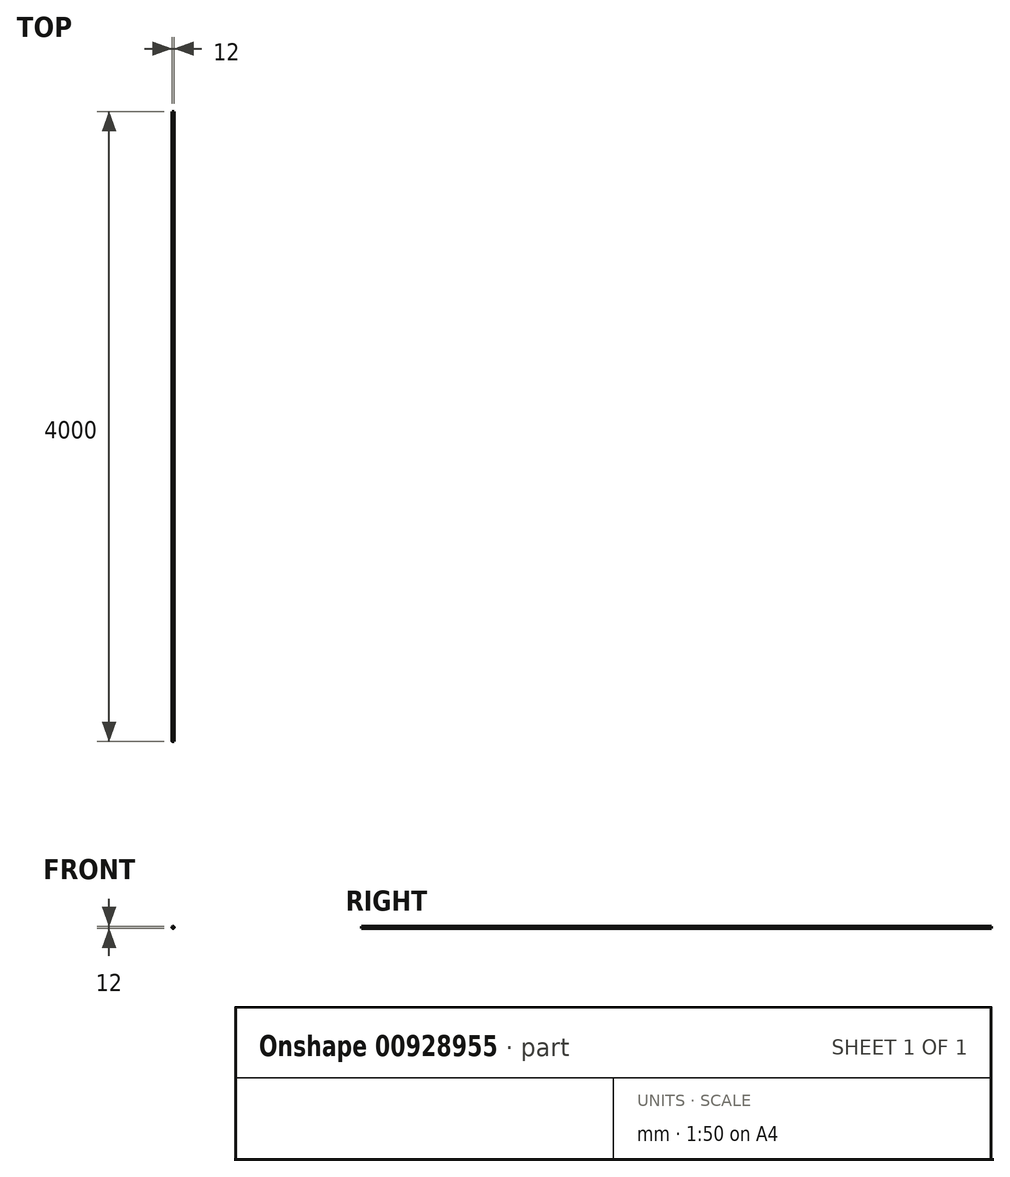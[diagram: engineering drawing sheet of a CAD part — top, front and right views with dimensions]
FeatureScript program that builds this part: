
annotation { "Feature Type Name" : "Feature", "Feature Type Description" : "" }
export const myFeature = defineFeature(function(context is Context, id is Id, definition is map)
    precondition{}
    {
        {
            var Q0;
            Q0=qCreatedBy(makeId("Front.planeOp"),FACE);
            var sketch = newSketch(context, id + "F0", { "sketchPlane" : qUnion([Q0])});
            skCircle(sketch, "E0", {"center": v(0, 0) * mm, "radius": 6 * mm});
            skSolve(sketch);
        }
        {
            var Q0;
            Q0 = qSketchRegion(id + "F0", true);
            extrude(context, id + "F1", {"entities" : qUnion([Q0]), "depth" : 4000 * mm, "offsetDistance" : 25.4 * mm});
        }
    });
